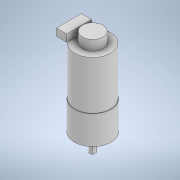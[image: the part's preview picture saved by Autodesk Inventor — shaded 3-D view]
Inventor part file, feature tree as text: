
AUTODESK INVENTOR PART (.ipt)
format: ipt  version: 2020.2 (Build 242310000, 310)  size: 174,080 bytes
history: native  units: mm
features: sketch x10, extrude x8, hole x1
ambient origin geometry x8: Origin, YZ Plane, XZ Plane, XY Plane, X Axis, Y Axis, Z Axis, Center Point
bodies: Solido1 (feature_tree)
feature tree (19):
  extrude  "Estrusione1"  Depth=24.4mm
  extrude  "Estrusione2"  Depth=31.0mm TaperAngle=0.0deg
  extrude  "Estrusione3"  Depth=25.0mm
  extrude  "Estrusione4"  Depth=19.5mm TaperAngle=0.0deg
  extrude  "Estrusione5"  Depth=7.0mm
  hole  "Foro1"  [1 undecoded]
  sketch  "Schizzo7"
  extrude  "Estrusione6"  Depth=4.0mm
  extrude  "Estrusione7"  Depth=9.5mm TaperAngle=0.0deg
  extrude  "Estrusione8"  Depth=3.5mm
  sketch  "Schizzo1"
  sketch  "Schizzo2"
  sketch  "Schizzo3"
  sketch  "Schizzo4"
  sketch  "Schizzo5"
  sketch  "Schizzo6"
  sketch  "Schizzo8"
  sketch  "Schizzo9"
  sketch  "Schizzo10"
note: 1 required parameter value undecoded (feature->parameter linkage not recoverable at this tier; creation-order binding heuristic only, values carry confidence <= 0.55)
